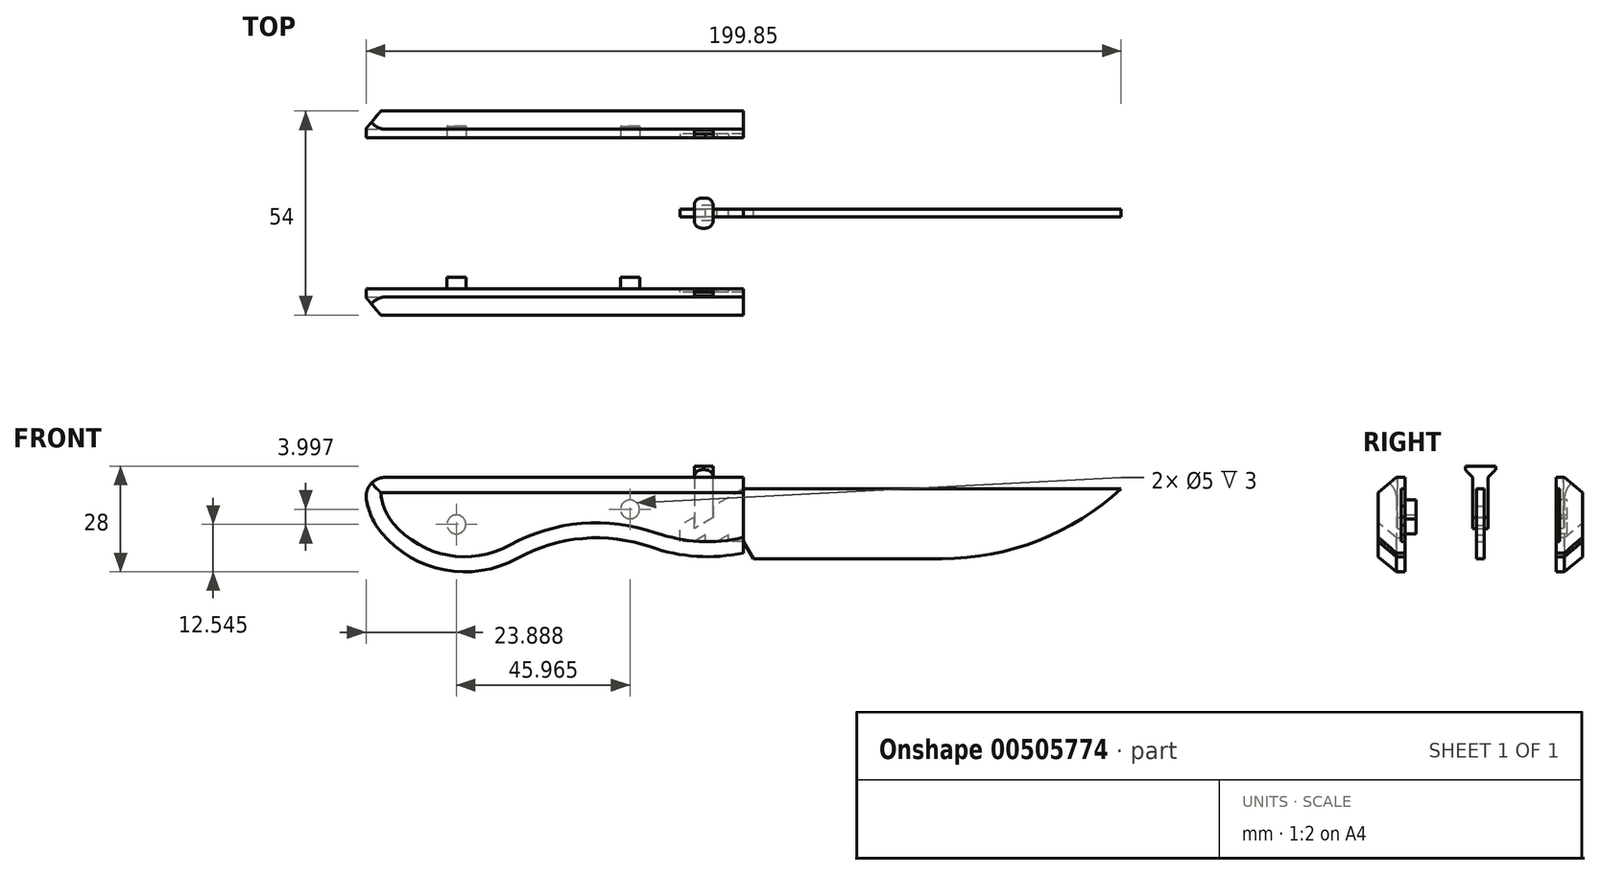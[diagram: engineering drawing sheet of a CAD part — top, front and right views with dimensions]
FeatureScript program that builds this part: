
annotation { "Feature Type Name" : "Feature", "Feature Type Description" : "" }
export const myFeature = defineFeature(function(context is Context, id is Id, definition is map)
    precondition{}
    {
        {
            var Q0;
            Q0=qCreatedBy(makeId("Front.planeOp"),FACE);
            cPlane(context, id + "F0", {"entities" : qUnion([Q0]), "cplaneType" : CPlaneType.OFFSET, "offset" : 20 * mm, "width" : 150 * mm, "height" : 150 * mm});
        }
        {
            var Q0;
            Q0=qCreatedBy(id+"F0.planeOp",FACE);
            var sketch = newSketch(context, id + "F1", { "sketchPlane" : qUnion([Q0])});
            skLineSegment(sketch, "E0", {"start": v(46.33, 7.51) * mm, "end": v(46.33, -12.49) * mm});
            skLineSegment(sketch, "E1", {"start": v(46.33, 7.51) * mm, "end": v(-53.67, 7.51) * mm});
            skLineSegment(sketch, "E2", {"start": v(-53.67, 7.51) * mm, "end": v(-53.67, 4.51) * mm});
            skArc(sketch, "E3", {"start": v(-53.67, 4.51) * mm, "mid": v(-52.57, -1.7) * mm, "end": v(-49.43, -7.18) * mm});
            skArc(sketch, "E4", {"start": v(-49.43, -7.18) * mm, "mid": v(-32.67, -17) * mm, "end": v(-13.5, -13.91) * mm});
            skArc(sketch, "E5", {"start": v(-13.5, -13.91) * mm, "mid": v(3.84, -8.66) * mm, "end": v(21.81, -10.93) * mm});
            skArc(sketch, "E6", {"start": v(21.81, -10.93) * mm, "mid": v(33.96, -13.4) * mm, "end": v(46.33, -12.49) * mm});
            skSolve(sketch);
        }
        {
            var Q0;
            Q0=makeQuery(id+"F1.imprint","IMPRINT",FACE,{"disambiguationData":[TD([[makeQuery(id+"F1.imprint","IMPRINT",EDGE,{"derivedFrom":sQuery(id+"F1.wireOp",EDGE,"E0")}),-1.0]])]});
            extrude(context, id + "F2", {"entities" : qUnion([Q0]), "depth" : 7 * mm});
        }
        {
            var Q0;
            Q0=makeQuery(id+"F2.opExtrude","CAP_EDGE",EDGE,{"disambiguationData":[OSD([sQuery(id+"F1.wireOp",EDGE,"E3")])],"isStart":false});
            chamfer(context, id + "F3", {"entities" : qUnion([Q0]), "chamferType" : ChamferType.OFFSET_ANGLE, "width" : 4 * mm, "oppositeDirection" : false, "angle" : 50 * degree, "tangentPropagation" : true});
        }
        {
            var Q0;
            Q0=makeQuery(id+"F2.opExtrude","CAP_EDGE",EDGE,{"disambiguationData":[OSD([sQuery(id+"F1.wireOp",EDGE,"E1")])],"isStart":false});
            chamfer(context, id + "F4", {"entities" : qUnion([Q0]), "chamferType" : ChamferType.OFFSET_ANGLE, "width" : 4 * mm, "oppositeDirection" : false, "angle" : 50 * degree, "tangentPropagation" : true});
        }
        {
            var Q0;
            Q0=makeQuery(id+"F2.opExtrude","SWEPT_EDGE",EDGE,{"disambiguationData":[OSD([sQuery(id+"F1.wireOp",EDGE,"E1"),sQuery(id+"F1.wireOp",EDGE,"E2")])]});
            fillet(context, id + "F5", {"entities" : qUnion([Q0]), "radius" : 5 * mm, "tangentPropagation" : true, "allowEdgeOverflow" : false});
        }
        {
            var Q0;
            Q0=makeQuery(id+"F2.opExtrude","CAP_FACE",FACE,{"disambiguationData":[OSD([sQuery(id+"F1.wireOp",EDGE,"E0"),sQuery(id+"F1.wireOp",EDGE,"E1"),sQuery(id+"F1.wireOp",EDGE,"E2"),sQuery(id+"F1.wireOp",EDGE,"E3"),sQuery(id+"F1.wireOp",EDGE,"E4"),sQuery(id+"F1.wireOp",EDGE,"E5"),sQuery(id+"F1.wireOp",EDGE,"E6")])],"isStart":true});
            var sketch = newSketch(context, id + "F6", { "sketchPlane" : qUnion([Q0])});
            skLineSegment(sketch, "E7", {"start": v(-46.33, 4.51) * mm, "end": v(-46.33, -9.49) * mm});
            skLineSegment(sketch, "E8", {"start": v(-46.33, -9.49) * mm, "end": v(-29.58, -9.49) * mm});
            skLineSegment(sketch, "E9", {"start": v(-29.58, -9.49) * mm, "end": v(-29.58, -5.16) * mm});
            skLineSegment(sketch, "E10", {"start": v(-38.33, -0.1) * mm, "end": v(-38.33, 7.51) * mm});
            skLineSegment(sketch, "E11", {"start": v(-33.33, 7.51) * mm, "end": v(-33.33, -3) * mm});
            skLineSegment(sketch, "E12", {"start": v(-46.33, 4.51) * mm, "end": v(-38.33, -0.1) * mm});
            skLineSegment(sketch, "E13", {"start": v(-42.33, -9.49) * mm, "end": v(-42.33, -7.75) * mm});
            skLineSegment(sketch, "E14", {"start": v(-42.33, -7.75) * mm, "end": v(-39.33, -9.49) * mm});
            skLineSegment(sketch, "E15", {"start": v(-36.33, -9.49) * mm, "end": v(-36.33, -7.75) * mm});
            skLineSegment(sketch, "E16", {"start": v(-36.33, -7.75) * mm, "end": v(-33.33, -9.49) * mm});
            skLineSegment(sketch, "E17.trimOffspring", {"start": v(-33.33, -3) * mm, "end": v(-29.58, -5.16) * mm});
            skLineSegment(sketch, "E18", {"start": v(-38.33, -0.1) * mm, "end": v(-33.33, -3) * mm});
            skLineSegment(sketch, "E19", {"start": v(-38.33, -0.1) * mm, "end": v(-38.33, -3.1) * mm});
            skLineSegment(sketch, "E20", {"start": v(-38.33, -3.1) * mm, "end": v(-33.33, -6) * mm});
            skLineSegment(sketch, "E21", {"start": v(-33.33, -6) * mm, "end": v(-33.33, -3) * mm});
            skSolve(sketch);
        }
        {
            var Q0;
            {var subQ4=sQuery(id+"F6.wireOp",EDGE,"E7");Q0=makeQuery(id+"F6.imprint","IMPRINT",FACE,{"disambiguationData":[TD([[makeQuery(id+"F6.imprint","IMPRINT",EDGE,{"derivedFrom":subQ4}),1.0]])]});}
            extrude(context, id + "F7", {"entities" : qUnion([Q0]), "operationType" : NewBodyOperationType.REMOVE, "oppositeDirection" : true, "depth" : 1 * mm});
        }
        {
            var Q0;
            {var subQ0=sQuery(id+"F6.wireOp",EDGE,"E10");Q0=makeQuery(id+"F6.imprint","IMPRINT",FACE,{"disambiguationData":[TD([[makeQuery(id+"F6.imprint","IMPRINT",EDGE,{"derivedFrom":subQ0}),-1.0]])]});}
            var Q1;
            Q1=makeQuery(id+"F6.imprint","IMPRINT",FACE,{"disambiguationData":[TD([[makeQuery(id+"F6.imprint","IMPRINT",EDGE,{"derivedFrom":sQuery(id+"F6.wireOp",EDGE,"E18")}),-1.0]])]});
            extrude(context, id + "F8", {"entities" : qUnion([Q0, Q1]), "operationType" : NewBodyOperationType.REMOVE, "oppositeDirection" : true, "depth" : 2 * mm});
        }
        {
            var Q0;
            Q0=makeQuery(id+"F2.opExtrude","SWEPT_BODY",BODY,{"disambiguationData":[OSD([sQuery(id+"F1.wireOp",EDGE,"E0"),sQuery(id+"F1.wireOp",EDGE,"E1"),sQuery(id+"F1.wireOp",EDGE,"E2"),sQuery(id+"F1.wireOp",EDGE,"E3"),sQuery(id+"F1.wireOp",EDGE,"E4"),sQuery(id+"F1.wireOp",EDGE,"E5"),sQuery(id+"F1.wireOp",EDGE,"E6")])]});
            var Q1;
            Q1=qCreatedBy(makeId("Front.planeOp"),FACE);
            mirror(context, id + "F9", {"entities" : qUnion([Q0]), "mirrorPlane" : qUnion([Q1])});
        }
        {
            var Q0;
            Q0=qCreatedBy(makeId("Front.planeOp"),FACE);
            var sketch = newSketch(context, id + "F10", { "sketchPlane" : qUnion([Q0])});
            skCircle(sketch, "E22", {"center": v(16.33, -0.95) * mm, "radius": 2.5 * mm});
            skCircle(sketch, "E23", {"center": v(-29.63, -4.95) * mm, "radius": 2.5 * mm});
            skLineSegment(sketch, "E24", {"start": v(16.33, 7.51) * mm, "end": v(16.33, -9.41) * mm, "construction": true});
            skLineSegment(sketch, "E25", {"start": v(-29.63, -17.4) * mm, "end": v(-29.63, 7.51) * mm, "construction": true});
            skSolve(sketch);
        }
        {
            var Q0;
            Q0=makeQuery(id+"F10.imprint","IMPRINT",FACE,{"disambiguationData":[TD([[makeQuery(id+"F10.imprint","IMPRINT",EDGE,{"derivedFrom":sQuery(id+"F10.wireOp",EDGE,"E22")}),1.0]])]});
            var Q1;
            Q1=makeQuery(id+"F10.imprint","IMPRINT",FACE,{"disambiguationData":[TD([[makeQuery(id+"F10.imprint","IMPRINT",EDGE,{"derivedFrom":sQuery(id+"F10.wireOp",EDGE,"E23")}),1.0]])]});
            extrude(context, id + "F11", {"entities" : qUnion([Q0, Q1]), "operationType" : NewBodyOperationType.ADD, "endBound" : BoundingType.SYMMETRIC, "oppositeDirection" : true, "depth" : 43 * mm});
        }
        {
            var Q0;
            Q0 = qSketchRegion(id + "F10", true);
            extrude(context, id + "F12", {"entities" : qUnion([Q0]), "operationType" : NewBodyOperationType.REMOVE, "oppositeDirection" : true, "depth" : 23 * mm});
        }
        {
            var Q0;
            Q0 = qSketchRegion(id + "F10", true);
            extrude(context, id + "F13", {"entities" : qUnion([Q0]), "operationType" : NewBodyOperationType.REMOVE, "depth" : 17 * mm});
        }
        {
            var Q0;
            Q0=qCreatedBy(makeId("Front.planeOp"),FACE);
            var sketch = newSketch(context, id + "F14", { "sketchPlane" : qUnion([Q0])});
            skLineSegment(sketch, "E26.0", {"start": v(46.33, 4.51) * mm, "end": v(38.33, -0.1) * mm});
            skLineSegment(sketch, "E27.0", {"start": v(46.33, 4.51) * mm, "end": v(46.33, -9.49) * mm});
            skLineSegment(sketch, "E28.0", {"start": v(46.33, -9.49) * mm, "end": v(42.33, -9.49) * mm});
            skLineSegment(sketch, "E29.0", {"start": v(42.33, -9.49) * mm, "end": v(42.33, -7.75) * mm});
            skPoint(sketch, "E30.0", {"position": v(40.83, -8.62) * mm});
            skLineSegment(sketch, "E31.0", {"start": v(42.33, -7.75) * mm, "end": v(39.33, -9.49) * mm});
            skLineSegment(sketch, "E32.0", {"start": v(36.33, -7.75) * mm, "end": v(33.33, -9.49) * mm});
            skLineSegment(sketch, "E33.0", {"start": v(36.33, -9.49) * mm, "end": v(36.33, -7.75) * mm});
            skLineSegment(sketch, "E34.0", {"start": v(29.58, -9.49) * mm, "end": v(29.58, -5.16) * mm});
            skLineSegment(sketch, "E35.0", {"start": v(33.33, -3) * mm, "end": v(29.58, -5.16) * mm});
            skLineSegment(sketch, "E36.0.2", {"start": v(33.33, -9.49) * mm, "end": v(29.58, -9.49) * mm});
            skLineSegment(sketch, "E36.0.4", {"start": v(29.58, -5.16) * mm, "end": v(33.33, -3) * mm});
            skLineSegment(sketch, "E36.0.5", {"start": v(33.33, -3) * mm, "end": v(33.33, -6) * mm});
            skLineSegment(sketch, "E36.0.6", {"start": v(33.33, -6) * mm, "end": v(38.33, -3.1) * mm});
            skLineSegment(sketch, "E36.0.7", {"start": v(38.33, -3.1) * mm, "end": v(38.33, -0.1) * mm});
            skLineSegment(sketch, "E36.0.8", {"start": v(38.33, -0.1) * mm, "end": v(46.33, 4.51) * mm});
            skLineSegment(sketch, "E36.0.13", {"start": v(39.33, -9.49) * mm, "end": v(36.33, -9.49) * mm});
            skLineSegment(sketch, "E37", {"start": v(46.33, 4.51) * mm, "end": v(146.33, 4.51) * mm});
            skLineSegment(sketch, "E38", {"start": v(46.33, -9.49) * mm, "end": v(48.94, -14) * mm});
            skLineSegment(sketch, "E39", {"start": v(48.94, -14) * mm, "end": v(98.94, -14) * mm});
            skArc(sketch, "E40", {"start": v(98.94, -14) * mm, "mid": v(124.38, -9.21) * mm, "end": v(146.33, 4.51) * mm});
            skSolve(sketch);
        }
        {
            var Q0;
            Q0=makeQuery(id+"F14.imprint","IMPRINT",FACE,{"disambiguationData":[TD([[makeQuery(id+"F14.imprint","IMPRINT",EDGE,{"derivedFrom":sQuery(id+"F14.wireOp",EDGE,"E27.0")}),1.0]])]});
            var Q1;
            Q1=makeQuery(id+"F14.imprint","IMPRINT",FACE,{"disambiguationData":[TD([[makeQuery(id+"F14.imprint","IMPRINT",EDGE,{"derivedFrom":sQuery(id+"F14.wireOp",EDGE,"E33.0")}),-1.0]])]});
            extrude(context, id + "F15", {"entities" : qUnion([Q0, Q1]), "endBound" : BoundingType.SYMMETRIC, "depth" : 2 * mm});
        }
        {
            var Q0;
            Q0=qCreatedBy(makeId("Front.planeOp"),FACE);
            var sketch = newSketch(context, id + "F16", { "sketchPlane" : qUnion([Q0])});
            skLineSegment(sketch, "E41.0", {"start": v(33.33, 7.51) * mm, "end": v(33.33, -3) * mm});
            skLineSegment(sketch, "E42.0", {"start": v(38.33, -0.1) * mm, "end": v(38.33, 7.51) * mm});
            skLineSegment(sketch, "E43.0", {"start": v(38.33, -0.1) * mm, "end": v(38.33, -3.1) * mm});
            skLineSegment(sketch, "E44.0", {"start": v(38.33, -3.1) * mm, "end": v(33.33, -6) * mm});
            skLineSegment(sketch, "E45.0", {"start": v(33.33, -6) * mm, "end": v(33.33, -3) * mm});
            skLineSegment(sketch, "E46.0", {"start": v(38.33, 7.51) * mm, "end": v(33.33, 7.51) * mm});
            skLineSegment(sketch, "E47", {"start": v(38.33, 7.51) * mm, "end": v(38.33, 10.51) * mm});
            skLineSegment(sketch, "E48", {"start": v(38.33, 10.51) * mm, "end": v(33.33, 10.51) * mm});
            skLineSegment(sketch, "E49", {"start": v(33.33, 10.51) * mm, "end": v(33.33, 7.51) * mm});
            skSolve(sketch);
        }
        {
            var Q0;
            Q0=makeQuery(id+"F16.imprint","IMPRINT",FACE,{"disambiguationData":[TD([[makeQuery(id+"F16.imprint","IMPRINT",EDGE,{"derivedFrom":sQuery(id+"F16.wireOp",EDGE,"E41.0")}),1.0]])]});
            extrude(context, id + "F17", {"entities" : qUnion([Q0]), "endBound" : BoundingType.SYMMETRIC, "depth" : 4 * mm});
        }
        {
            var Q0;
            Q0=makeQuery(id+"F16.imprint","IMPRINT",FACE,{"disambiguationData":[TD([[makeQuery(id+"F16.imprint","IMPRINT",EDGE,{"derivedFrom":sQuery(id+"F16.wireOp",EDGE,"E46.0")}),-1.0]])]});
            extrude(context, id + "F18", {"entities" : qUnion([Q0]), "operationType" : NewBodyOperationType.ADD, "endBound" : BoundingType.SYMMETRIC, "depth" : 8 * mm});
        }
        {
            var Q0;
            Q0=makeQuery(id+"F18.opExtrude","CAP_EDGE",EDGE,{"disambiguationData":[OSD([sQuery(id+"F16.wireOp",EDGE,"E47")])],"isStart":false});
            var Q1;
            Q1=makeQuery(id+"F18.opExtrude","CAP_EDGE",EDGE,{"disambiguationData":[OSD([sQuery(id+"F16.wireOp",EDGE,"E47")])],"isStart":true});
            var Q2;
            Q2=makeQuery(id+"F18.opExtrude","CAP_EDGE",EDGE,{"disambiguationData":[OSD([sQuery(id+"F16.wireOp",EDGE,"E49")])],"isStart":true});
            var Q3;
            Q3=makeQuery(id+"F18.opExtrude","CAP_EDGE",EDGE,{"disambiguationData":[OSD([sQuery(id+"F16.wireOp",EDGE,"E49")])],"isStart":false});
            fillet(context, id + "F19", {"entities" : qUnion([Q0, Q1, Q2, Q3]), "radius" : 2 * mm, "tangentPropagation" : true, "allowEdgeOverflow" : false});
        }
        {
            var Q0;
            {var subQ2=sQuery(id+"F16.wireOp",EDGE,"E49");var subQ3=sQuery(id+"F16.wireOp",EDGE,"E47");var subQ4=sQuery(id+"F16.wireOp",EDGE,"E46.0");Q0=makeQuery(id+"F19.opFillet","BLEND_EDGE",EDGE,{"blendedFrom":[makeQuery(id+"F18.opExtrude","CAP_EDGE",EDGE,{"disambiguationData":[OSD([subQ3])],"isStart":true}),makeQuery(id+"F18.boolean.opBoolean","SPLIT",FACE,{"disambiguationData":[TD([makeQuery(id+"F18.opExtrude","CAP_FACE",FACE,{"disambiguationData":[OSD([subQ4,subQ3,sQuery(id+"F16.wireOp",EDGE,"E48"),subQ2])],"isStart":true})])],"derivedFrom":makeQuery(id+"F18.opExtrude","SWEPT_FACE",FACE,{"disambiguationData":[OSD([subQ4])]})})],"blendedInto":[makeQuery(id+"F18.boolean.opBoolean","SPLIT",FACE,{"disambiguationData":[TD([makeQuery(id+"F18.opExtrude","CAP_FACE",FACE,{"disambiguationData":[OSD([subQ4,subQ3,sQuery(id+"F16.wireOp",EDGE,"E48"),subQ2])],"isStart":true})])],"derivedFrom":makeQuery(id+"F18.opExtrude","SWEPT_FACE",FACE,{"disambiguationData":[OSD([subQ4])]})})]});}
            var Q1;
            {var subQ0=sQuery(id+"F16.wireOp",EDGE,"E49");var subQ1=sQuery(id+"F16.wireOp",EDGE,"E47");var subQ2=sQuery(id+"F16.wireOp",EDGE,"E46.0");Q1=makeQuery(id+"F19.opFillet","BLEND_EDGE",EDGE,{"blendedFrom":[makeQuery(id+"F18.opExtrude","CAP_EDGE",EDGE,{"disambiguationData":[OSD([subQ1])],"isStart":false}),makeQuery(id+"F18.boolean.opBoolean","SPLIT",FACE,{"disambiguationData":[TD([makeQuery(id+"F18.opExtrude","CAP_FACE",FACE,{"disambiguationData":[OSD([subQ2,subQ1,sQuery(id+"F16.wireOp",EDGE,"E48"),subQ0])],"isStart":false})])],"derivedFrom":makeQuery(id+"F18.opExtrude","SWEPT_FACE",FACE,{"disambiguationData":[OSD([subQ2])]})})],"blendedInto":[makeQuery(id+"F18.boolean.opBoolean","SPLIT",FACE,{"disambiguationData":[TD([makeQuery(id+"F18.opExtrude","CAP_FACE",FACE,{"disambiguationData":[OSD([subQ2,subQ1,sQuery(id+"F16.wireOp",EDGE,"E48"),subQ0])],"isStart":false})])],"derivedFrom":makeQuery(id+"F18.opExtrude","SWEPT_FACE",FACE,{"disambiguationData":[OSD([subQ2])]})})]});}
            chamfer(context, id + "F20", {"entities" : qUnion([Q0, Q1]), "width" : 2 * mm, "tangentPropagation" : true});
        }
    });
